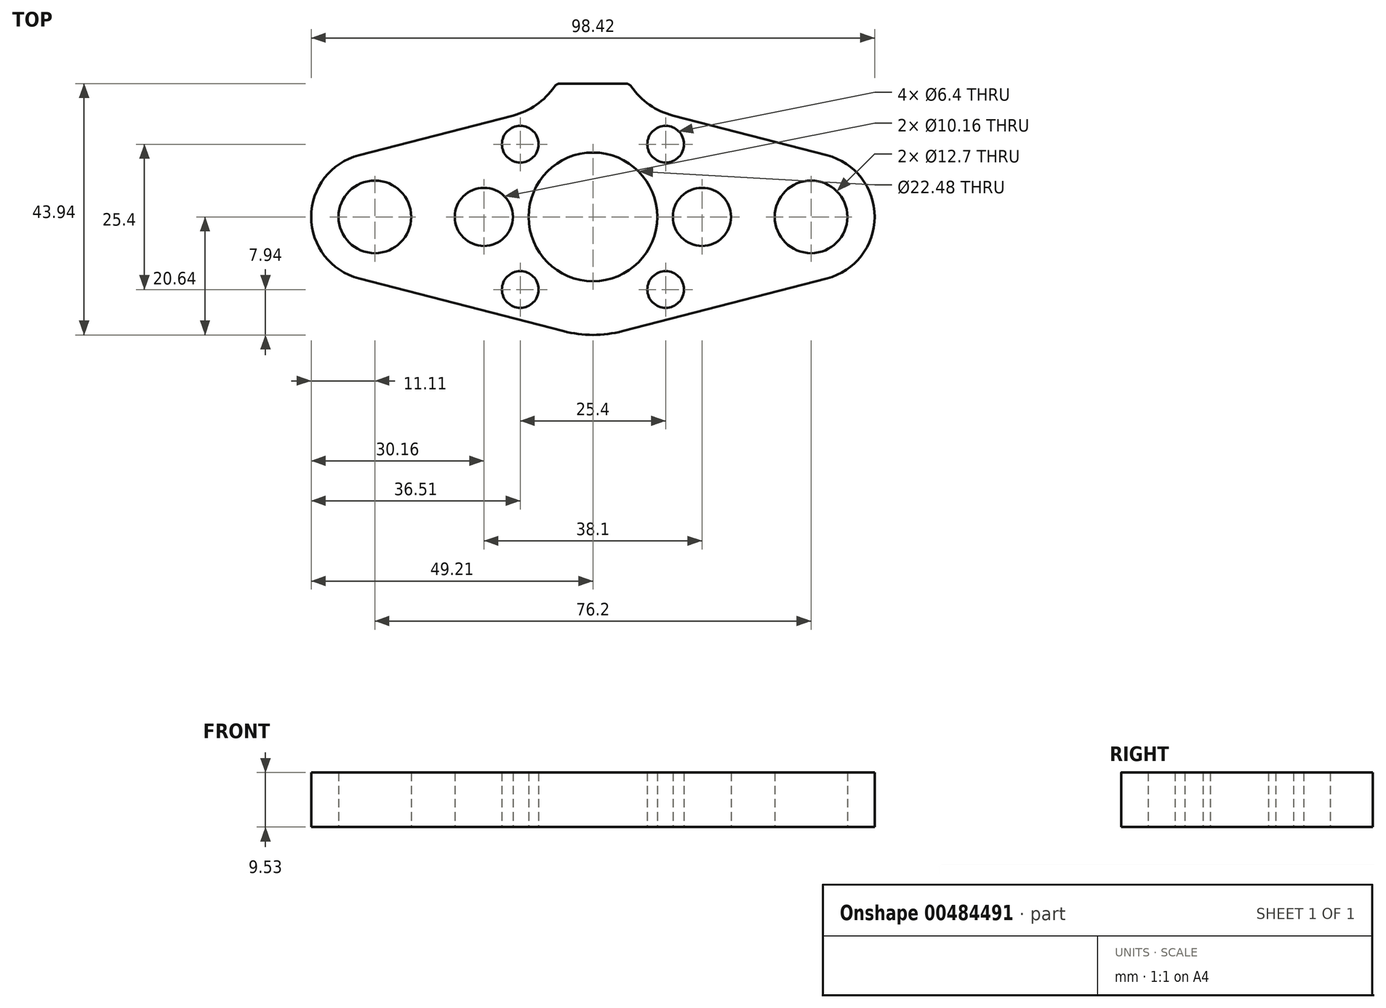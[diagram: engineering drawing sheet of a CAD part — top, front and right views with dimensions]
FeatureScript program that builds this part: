
annotation { "Feature Type Name" : "Feature", "Feature Type Description" : "" }
export const myFeature = defineFeature(function(context is Context, id is Id, definition is map)
    precondition{}
    {
        {
            var Q0;
            Q0=qCreatedBy(makeId("Top.planeOp"),FACE);
            var sketch = newSketch(context, id + "F0", { "sketchPlane" : qUnion([Q0])});
            skCircle(sketch, "E0", {"center": v(0, 0) * mm, "radius": 11.24 * mm});
            skCircle(sketch, "E1", {"center": v(-19.05, 0) * mm, "radius": 5.08 * mm});
            skCircle(sketch, "E2", {"center": v(19.05, 0) * mm, "radius": 5.08 * mm});
            skLineSegment(sketch, "E3", {"start": v(-19.05, 0) * mm, "end": v(19.05, 0) * mm, "construction": true});
            skCircle(sketch, "E4", {"center": v(-38.1, 0) * mm, "radius": 6.35 * mm});
            skCircle(sketch, "E5", {"center": v(38.1, 0) * mm, "radius": 6.35 * mm});
            skLineSegment(sketch, "E6", {"start": v(-19.05, 0) * mm, "end": v(-38.1, 0) * mm, "construction": true});
            skLineSegment(sketch, "E7", {"start": v(19.05, 0) * mm, "end": v(38.1, 0) * mm, "construction": true});
            skArc(sketch, "E8", {"start": v(-40.88, 10.76) * mm, "mid": v(-49.21, 0) * mm, "end": v(-40.88, -10.76) * mm});
            skArc(sketch, "E9", {"start": v(40.88, -10.76) * mm, "mid": v(49.21, 0) * mm, "end": v(40.88, 10.76) * mm});
            skArc(sketch, "E10", {"start": v(-5.16, -19.98) * mm, "mid": v(0, -20.64) * mm, "end": v(5.16, -19.98) * mm});
            skLineSegment(sketch, "E11", {"start": v(-40.88, 10.76) * mm, "end": v(-5.16, 19.98) * mm});
            skLineSegment(sketch, "E12", {"start": v(5.16, 19.98) * mm, "end": v(40.88, 10.76) * mm});
            skLineSegment(sketch, "E13", {"start": v(-40.88, -10.76) * mm, "end": v(-5.16, -19.98) * mm});
            skLineSegment(sketch, "E14", {"start": v(5.16, -19.98) * mm, "end": v(40.88, -10.76) * mm});
            skArc(sketch, "E15.trimOffspring", {"start": v(5.16, 19.98) * mm, "mid": v(0, 20.64) * mm, "end": v(-5.16, 19.98) * mm});
            skLineSegment(sketch, "E16.bottom", {"start": v(-12.7, 12.7) * mm, "end": v(12.7, 12.7) * mm, "construction": true});
            skLineSegment(sketch, "E16.top", {"start": v(-12.7, -12.7) * mm, "end": v(12.7, -12.7) * mm, "construction": true});
            skLineSegment(sketch, "E16.left", {"start": v(-12.7, 12.7) * mm, "end": v(-12.7, -12.7) * mm, "construction": true});
            skLineSegment(sketch, "E16.right", {"start": v(12.7, 12.7) * mm, "end": v(12.7, -12.7) * mm, "construction": true});
            skCircle(sketch, "E17", {"center": v(-12.7, 12.7) * mm, "radius": 3.2 * mm});
            skCircle(sketch, "E18", {"center": v(-12.7, -12.7) * mm, "radius": 3.2 * mm});
            skCircle(sketch, "E19", {"center": v(12.7, -12.7) * mm, "radius": 3.2 * mm});
            skCircle(sketch, "E20", {"center": v(12.7, 12.7) * mm, "radius": 3.2 * mm});
            skSolve(sketch);
        }
        {
            var Q0;
            Q0=qSketchRegion(id+"F0",true);
            extrude(context, id + "F1", {"entities" : qUnion([Q0]), "offsetDistance" : 25.4 * mm, "depth" : 9.52 * mm});
        }
        {
            var Q0;
            Q0=makeQuery(id+"F1.opExtrude","CAP_FACE",FACE,{"disambiguationData":[OSD([sQuery(id+"F0.wireOp",EDGE,"E0"),sQuery(id+"F0.wireOp",EDGE,"E1"),sQuery(id+"F0.wireOp",EDGE,"E2"),sQuery(id+"F0.wireOp",EDGE,"E4"),sQuery(id+"F0.wireOp",EDGE,"E5"),sQuery(id+"F0.wireOp",EDGE,"E8"),sQuery(id+"F0.wireOp",EDGE,"E9"),sQuery(id+"F0.wireOp",EDGE,"E10"),sQuery(id+"F0.wireOp",EDGE,"E11"),sQuery(id+"F0.wireOp",EDGE,"E12"),sQuery(id+"F0.wireOp",EDGE,"E13"),sQuery(id+"F0.wireOp",EDGE,"E14"),sQuery(id+"F0.wireOp",EDGE,"E15.trimOffspring"),sQuery(id+"F0.wireOp",EDGE,"E17"),sQuery(id+"F0.wireOp",EDGE,"E18"),sQuery(id+"F0.wireOp",EDGE,"E19"),sQuery(id+"F0.wireOp",EDGE,"E20")])],"isStart":false});
            var sketch = newSketch(context, id + "F2", { "sketchPlane" : qUnion([Q0])});
            skLineSegment(sketch, "E21", {"start": v(-6.35, 23.3) * mm, "end": v(6.35, 23.3) * mm});
            skLineSegment(sketch, "E22", {"start": v(0, 23.3) * mm, "end": v(0, 0) * mm, "construction": true});
            skLineSegment(sketch, "E23", {"start": v(-6.35, 23.3) * mm, "end": v(-6.35, 18.2) * mm});
            skLineSegment(sketch, "E24", {"start": v(-6.35, 18.2) * mm, "end": v(6.35, 18.2) * mm});
            skLineSegment(sketch, "E25", {"start": v(6.35, 18.2) * mm, "end": v(6.35, 23.3) * mm});
            skSolve(sketch);
        }
        {
            var Q0;
            Q0=qSketchRegion(id+"F2",true);
            var Q1;
            Q1=makeQuery(id+"F1.opExtrude","CAP_FACE",FACE,{"disambiguationData":[OSD([sQuery(id+"F0.wireOp",EDGE,"E0"),sQuery(id+"F0.wireOp",EDGE,"E1"),sQuery(id+"F0.wireOp",EDGE,"E2"),sQuery(id+"F0.wireOp",EDGE,"E4"),sQuery(id+"F0.wireOp",EDGE,"E5"),sQuery(id+"F0.wireOp",EDGE,"E8"),sQuery(id+"F0.wireOp",EDGE,"E9"),sQuery(id+"F0.wireOp",EDGE,"E10"),sQuery(id+"F0.wireOp",EDGE,"E11"),sQuery(id+"F0.wireOp",EDGE,"E12"),sQuery(id+"F0.wireOp",EDGE,"E13"),sQuery(id+"F0.wireOp",EDGE,"E14"),sQuery(id+"F0.wireOp",EDGE,"E15.trimOffspring"),sQuery(id+"F0.wireOp",EDGE,"E17"),sQuery(id+"F0.wireOp",EDGE,"E18"),sQuery(id+"F0.wireOp",EDGE,"E19"),sQuery(id+"F0.wireOp",EDGE,"E20")])],"isStart":true});
            extrude(context, id + "F3", {"entities" : qUnion([Q0]), "operationType" : NewBodyOperationType.ADD, "endBound" : BoundingType.UP_TO_SURFACE, "oppositeDirection" : true, "endBoundEntityFace" : qUnion([Q1]), "offsetDistance" : 25.4 * mm, "depth" : 6.35 * mm});
        }
        {
            var Q0;
            Q0=makeQuery(id+"F3.boolean.opBoolean","INTERSECT",EDGE,{"derivedFrom":[makeQuery(id+"F1.opExtrude","SWEPT_FACE",FACE,{"disambiguationData":[OSD([sQuery(id+"F0.wireOp",EDGE,"E11")])]}),makeQuery(id+"F3.opExtrude","SWEPT_FACE",FACE,{"disambiguationData":[OSD([sQuery(id+"F2.wireOp",EDGE,"E23")])]})]});
            var Q1;
            Q1=makeQuery(id+"F3.boolean.opBoolean","INTERSECT",EDGE,{"derivedFrom":[makeQuery(id+"F1.opExtrude","SWEPT_FACE",FACE,{"disambiguationData":[OSD([sQuery(id+"F0.wireOp",EDGE,"E12")])]}),makeQuery(id+"F3.opExtrude","SWEPT_FACE",FACE,{"disambiguationData":[OSD([sQuery(id+"F2.wireOp",EDGE,"E25")])]})]});
            fillet(context, id + "F4", {"entities" : qUnion([Q0, Q1]), "radius" : 12.7 * mm, "tangentPropagation" : true, "allowEdgeOverflow" : false});
        }
        {
            var Q0;
            Q0=makeQuery(id+"F4.opFillet","BLEND_EDGE",EDGE,{"blendedFrom":[makeQuery(id+"F3.boolean.opBoolean","INTERSECT",EDGE,{"derivedFrom":[makeQuery(id+"F1.opExtrude","SWEPT_FACE",FACE,{"disambiguationData":[OSD([sQuery(id+"F0.wireOp",EDGE,"E11")])]}),makeQuery(id+"F3.opExtrude","SWEPT_FACE",FACE,{"disambiguationData":[OSD([sQuery(id+"F2.wireOp",EDGE,"E23")])]})]}),makeQuery(id+"F3.opExtrude","SWEPT_FACE",FACE,{"disambiguationData":[OSD([sQuery(id+"F2.wireOp",EDGE,"E21")])]})],"blendedInto":[makeQuery(id+"F3.opExtrude","SWEPT_FACE",FACE,{"disambiguationData":[OSD([sQuery(id+"F2.wireOp",EDGE,"E21")])]})]});
            var Q1;
            Q1=makeQuery(id+"F4.opFillet","BLEND_EDGE",EDGE,{"blendedFrom":[makeQuery(id+"F3.boolean.opBoolean","INTERSECT",EDGE,{"derivedFrom":[makeQuery(id+"F1.opExtrude","SWEPT_FACE",FACE,{"disambiguationData":[OSD([sQuery(id+"F0.wireOp",EDGE,"E12")])]}),makeQuery(id+"F3.opExtrude","SWEPT_FACE",FACE,{"disambiguationData":[OSD([sQuery(id+"F2.wireOp",EDGE,"E25")])]})]}),makeQuery(id+"F3.opExtrude","SWEPT_FACE",FACE,{"disambiguationData":[OSD([sQuery(id+"F2.wireOp",EDGE,"E21")])]})],"blendedInto":[makeQuery(id+"F3.opExtrude","SWEPT_FACE",FACE,{"disambiguationData":[OSD([sQuery(id+"F2.wireOp",EDGE,"E21")])]})]});
            fillet(context, id + "F5", {"entities" : qUnion([Q0, Q1]), "radius" : 1.27 * mm, "tangentPropagation" : true, "allowEdgeOverflow" : false});
        }
    });
